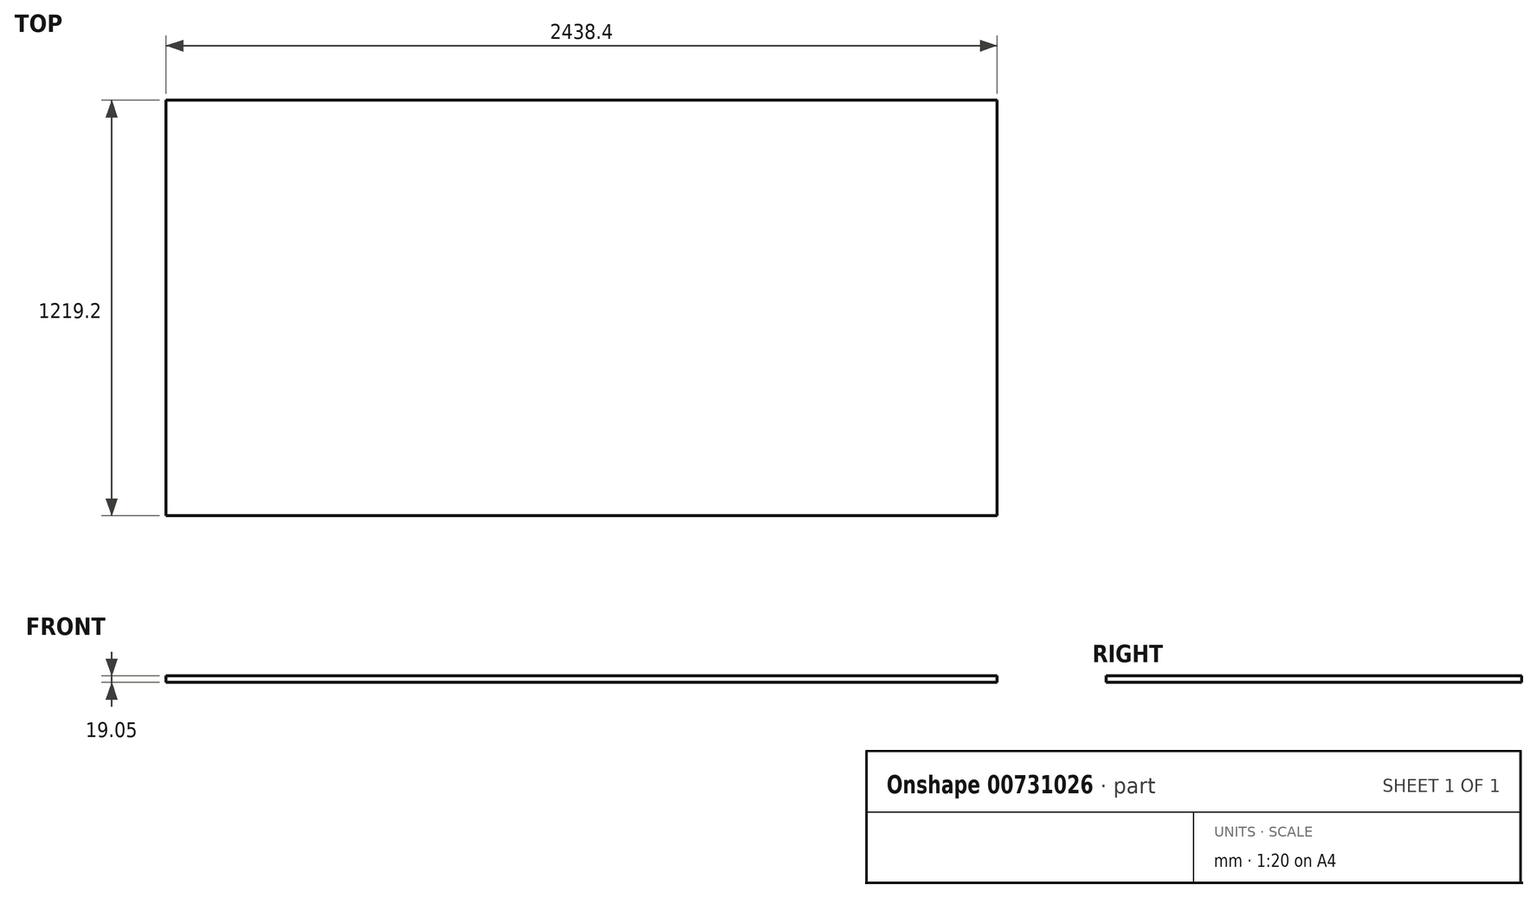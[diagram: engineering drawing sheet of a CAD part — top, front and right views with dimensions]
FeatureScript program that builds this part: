
annotation { "Feature Type Name" : "Feature", "Feature Type Description" : "" }
export const myFeature = defineFeature(function(context is Context, id is Id, definition is map)
    precondition{}
    {
        {
            var Q0;
            Q0=qCreatedBy(makeId("Top.planeOp"),FACE);
            var sketch = newSketch(context, id + "F0", { "sketchPlane" : qUnion([Q0])});
            skLineSegment(sketch, "E0.bottom", {"start": v(-1219.2, 609.6) * mm, "end": v(1219.2, 609.6) * mm});
            skLineSegment(sketch, "E0.top", {"start": v(-1219.2, -609.6) * mm, "end": v(1219.2, -609.6) * mm});
            skLineSegment(sketch, "E0.left", {"start": v(-1219.2, 609.6) * mm, "end": v(-1219.2, -609.6) * mm});
            skLineSegment(sketch, "E0.right", {"start": v(1219.2, 609.6) * mm, "end": v(1219.2, -609.6) * mm});
            skPoint(sketch, "E0.middle", {"position": v(0, 0) * mm});
            skSolve(sketch);
        }
        {
            var Q0;
            Q0 = qSketchRegion(id + "F0", true);
            extrude(context, id + "F1", {"entities" : qUnion([Q0]), "depth" : 19.05 * mm, "offsetDistance" : 25.4 * mm});
        }
    });
